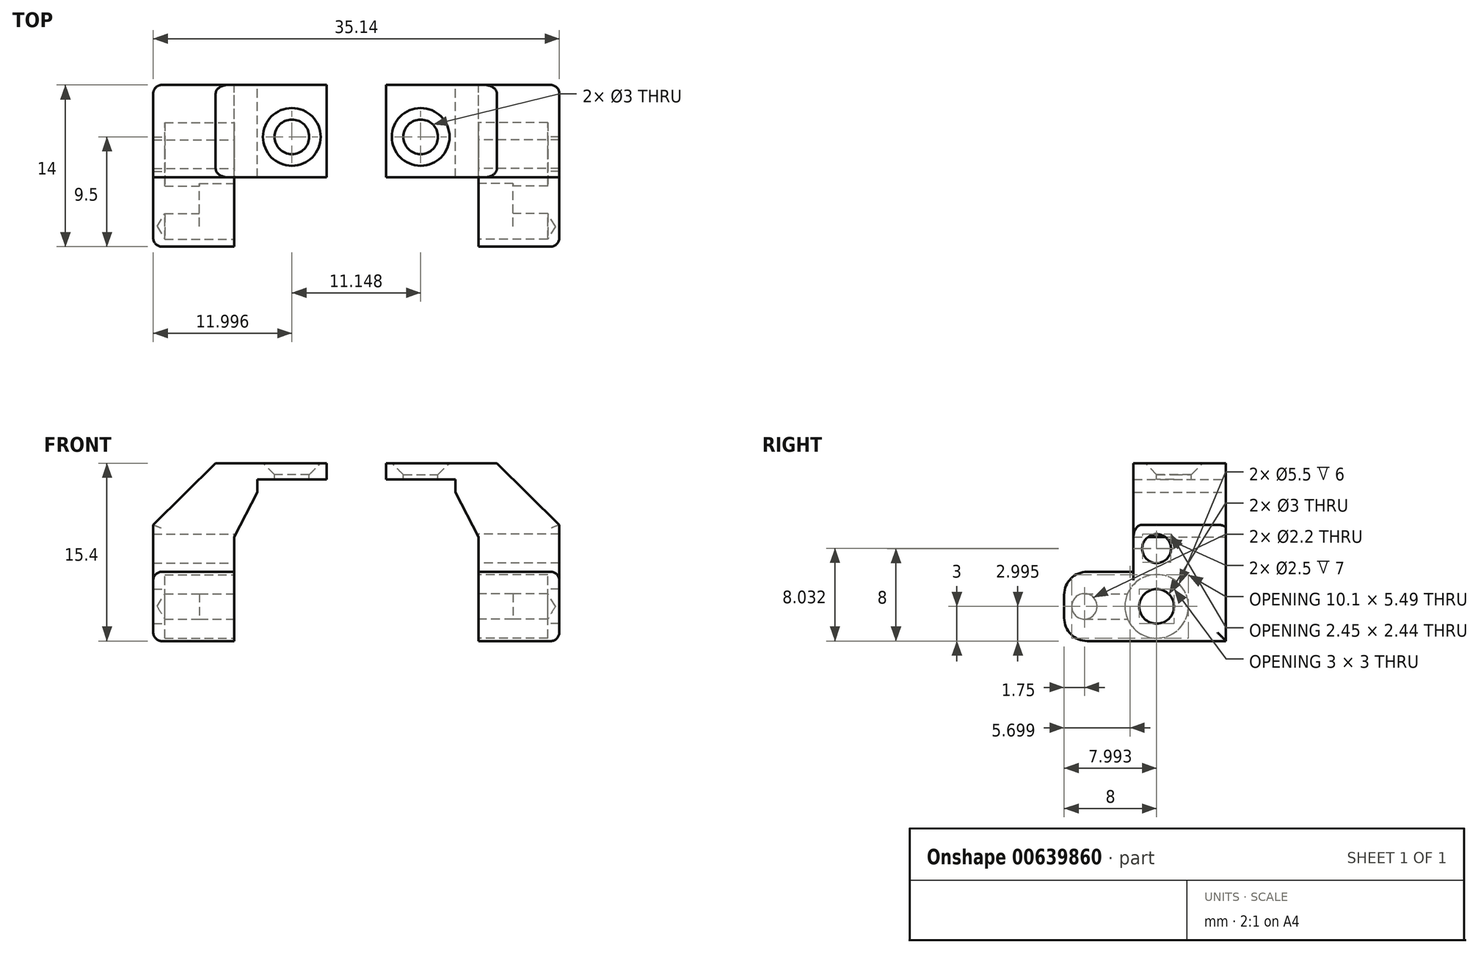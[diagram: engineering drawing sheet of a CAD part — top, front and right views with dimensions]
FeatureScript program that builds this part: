
annotation { "Feature Type Name" : "Feature", "Feature Type Description" : "" }
export const myFeature = defineFeature(function(context is Context, id is Id, definition is map)
    precondition{}
    {
        {
            var Q0;
            Q0=qCreatedBy(makeId("Front.planeOp"),FACE);
            var sketch = newSketch(context, id + "F0", { "sketchPlane" : qUnion([Q0])});
            skLineSegment(sketch, "E0", {"start": v(-10.57, 0) * mm, "end": v(-17.57, 0) * mm});
            skLineSegment(sketch, "E1", {"start": v(-17.57, 0) * mm, "end": v(-17.57, 10.07) * mm});
            skLineSegment(sketch, "E2", {"start": v(-17.57, 10.07) * mm, "end": v(-12.17, 15.4) * mm});
            skLineSegment(sketch, "E3", {"start": v(-12.17, 15.4) * mm, "end": v(-2.57, 15.4) * mm});
            skLineSegment(sketch, "E4", {"start": v(-2.57, 15.4) * mm, "end": v(-2.57, 14) * mm});
            skLineSegment(sketch, "E5", {"start": v(-2.57, 14) * mm, "end": v(-8.57, 14) * mm});
            skLineSegment(sketch, "E6", {"start": v(-10.57, 9) * mm, "end": v(-10.57, 0) * mm});
            skLineSegment(sketch, "E7", {"start": v(-8.57, 14) * mm, "end": v(-8.57, 12.88) * mm});
            skLineSegment(sketch, "E8", {"start": v(-8.57, 12.88) * mm, "end": v(-10.57, 9) * mm});
            skSolve(sketch);
        }
        {
            var Q0;
            Q0 = qSketchRegion(id + "F0", true);
            extrude(context, id + "F1", {"entities" : qUnion([Q0]), "depth" : 8 * mm, "offsetDistance" : 25 * mm});
        }
        {
            var Q0;
            Q0=makeQuery(id+"F1.opExtrude","SWEPT_FACE",FACE,{"disambiguationData":[OSD([sQuery(id+"F0.wireOp",EDGE,"E3")])]});
            var sketch = newSketch(context, id + "F2", { "sketchPlane" : qUnion([Q0])});
            skPoint(sketch, "E9.endSnap0", {"position": v(-5.57, -8) * mm});
            skLineSegment(sketch, "E10", {"start": v(-5.57, -8) * mm, "end": v(-5.57, -4.5) * mm});
            skCircle(sketch, "E11", {"center": v(-5.57, -4.5) * mm, "radius": 1.5 * mm});
            skSolve(sketch);
        }
        {
            var Q0;
            Q0=sQuery(id+"F2.wireOp",VERTEX,"E10.end");
            var Q1;
            Q1=makeQuery(id+"F1.opExtrude","SWEPT_BODY",BODY,{"disambiguationData":[OSD([sQuery(id+"F0.wireOp",EDGE,"E0"),sQuery(id+"F0.wireOp",EDGE,"E1"),sQuery(id+"F0.wireOp",EDGE,"E2"),sQuery(id+"F0.wireOp",EDGE,"E3"),sQuery(id+"F0.wireOp",EDGE,"E4"),sQuery(id+"F0.wireOp",EDGE,"E5"),sQuery(id+"F0.wireOp",EDGE,"E6"),sQuery(id+"F0.wireOp",EDGE,"E7"),sQuery(id+"F0.wireOp",EDGE,"E8")])]});
            hole(context, id + "F3", {"style" : HoleStyle.C_SINK, "endStyle" : HoleEndStyle.THROUGH, "holeDiameter" : 3 * mm, "cSinkDiameter" : 5 * mm, "cSinkAngle" : 90 * degree, "majorDiameter" : 5 * mm, "isTappedThrough" : true, "tappedDepth" : 12 * mm, "tapClearance" : 3, "locations" : qUnion([Q0]), "scope" : qUnion([Q1])});
        }
        {
            var Q0;
            Q0=makeQuery(id+"F1.opExtrude","SWEPT_FACE",FACE,{"disambiguationData":[OSD([sQuery(id+"F0.wireOp",EDGE,"E6")])]});
            var sketch = newSketch(context, id + "F4", { "sketchPlane" : qUnion([Q0])});
            skLineSegment(sketch, "E12", {"start": v(-8, 3) * mm, "end": v(-6, 3) * mm});
            skLineSegment(sketch, "E13", {"start": v(-6, 3) * mm, "end": v(-12.25, 3) * mm});
            skPoint(sketch, "E14", {"position": v(-12.25, 3) * mm});
            skCircle(sketch, "E15", {"center": v(-12.25, 3) * mm, "radius": 1.1 * mm});
            skLineSegment(sketch, "E16", {"start": v(-12.25, 4.1) * mm, "end": v(-6, 4.1) * mm});
            skLineSegment(sketch, "E17", {"start": v(-12.25, 1.9) * mm, "end": v(-6, 1.9) * mm});
            skLineSegment(sketch, "E18", {"start": v(-6, 1.9) * mm, "end": v(-6, 4.1) * mm});
            skLineSegment(sketch, "E19", {"start": v(-6, 3) * mm, "end": v(-6, 8) * mm});
            skSolve(sketch);
        }
        {
            var Q0;
            Q0=makeQuery(id+"F1.opExtrude","CAP_FACE",FACE,{"disambiguationData":[OSD([sQuery(id+"F0.wireOp",EDGE,"E0"),sQuery(id+"F0.wireOp",EDGE,"E1"),sQuery(id+"F0.wireOp",EDGE,"E2"),sQuery(id+"F0.wireOp",EDGE,"E3"),sQuery(id+"F0.wireOp",EDGE,"E4"),sQuery(id+"F0.wireOp",EDGE,"E5"),sQuery(id+"F0.wireOp",EDGE,"E6"),sQuery(id+"F0.wireOp",EDGE,"E7"),sQuery(id+"F0.wireOp",EDGE,"E8")])],"isStart":false});
            var sketch = newSketch(context, id + "F5", { "sketchPlane" : qUnion([Q0])});
            skLineSegment(sketch, "E20", {"start": v(-10.57, 6) * mm, "end": v(-17.57, 6) * mm});
            skSolve(sketch);
        }
        {
            var Q0;
            {var subQ0=sQuery(id+"F5.wireOp",EDGE,"E20");Q0=makeQuery(id+"F5.imprint","IMPRINT",FACE,{"disambiguationData":[TD([[makeQuery(id+"F5.imprint","IMPRINT",EDGE,{"derivedFrom":subQ0}),1.0]])]});}
            extrude(context, id + "F6", {"entities" : qUnion([Q0]), "operationType" : NewBodyOperationType.ADD, "depth" : 6 * mm, "offsetDistance" : 25 * mm});
        }
        {
            var Q0;
            Q0=sQuery(id+"F4.wireOp",VERTEX,"E12.end");
            var Q1;
            Q1=makeQuery(id+"F1.opExtrude","SWEPT_BODY",BODY,{"disambiguationData":[OSD([sQuery(id+"F0.wireOp",EDGE,"E0"),sQuery(id+"F0.wireOp",EDGE,"E1"),sQuery(id+"F0.wireOp",EDGE,"E2"),sQuery(id+"F0.wireOp",EDGE,"E3"),sQuery(id+"F0.wireOp",EDGE,"E4"),sQuery(id+"F0.wireOp",EDGE,"E5"),sQuery(id+"F0.wireOp",EDGE,"E6"),sQuery(id+"F0.wireOp",EDGE,"E7"),sQuery(id+"F0.wireOp",EDGE,"E8")])]});
            hole(context, id + "F7", {"style" : HoleStyle.C_BORE, "endStyle" : HoleEndStyle.THROUGH, "holeDiameter" : 3 * mm, "cBoreDiameter" : 5.5 * mm, "cBoreDepth" : 6 * mm, "majorDiameter" : 5 * mm, "isTappedThrough" : true, "tappedDepth" : 12 * mm, "tapClearance" : 3, "locations" : qUnion([Q0]), "scope" : qUnion([Q1])});
        }
        {
            var Q0;
            {var subQ0=sQuery(id+"F4.wireOp",EDGE,"E13");var subQ1=makeQuery(id+"F1.opExtrude","CAP_EDGE",EDGE,{"disambiguationData":[OSD([sQuery(id+"F0.wireOp",EDGE,"E6")])],"isStart":false});var subQ2=makeQuery(id+"F4.imprint","INTERSECT",VERTEX,{"derivedFrom":[subQ1,subQ0]});Q0=makeQuery(id+"F4.imprint","IMPRINT",FACE,{"disambiguationData":[TD([[makeQuery(id+"F4.imprint","IMPRINT",EDGE,{"disambiguationData":[TD([[subQ2,-1.0]])],"derivedFrom":subQ0}),-1.0]])]});}
            var Q1;
            {var subQ0=sQuery(id+"F4.wireOp",EDGE,"E13");var subQ1=makeQuery(id+"F1.opExtrude","CAP_EDGE",EDGE,{"disambiguationData":[OSD([sQuery(id+"F0.wireOp",EDGE,"E6")])],"isStart":false});var subQ2=makeQuery(id+"F4.imprint","INTERSECT",VERTEX,{"derivedFrom":[subQ1,subQ0]});Q1=makeQuery(id+"F4.imprint","IMPRINT",FACE,{"disambiguationData":[TD([[makeQuery(id+"F4.imprint","IMPRINT",EDGE,{"disambiguationData":[TD([[subQ2,-1.0]])],"derivedFrom":subQ0}),1.0]])]});}
            extrude(context, id + "F8", {"entities" : qUnion([Q0, Q1]), "operationType" : NewBodyOperationType.REMOVE, "oppositeDirection" : true, "depth" : 3 * mm, "offsetDistance" : 25 * mm});
        }
        {
            var Q0;
            Q0=sQuery(id+"F4.wireOp",VERTEX,"E14");
            var Q1;
            Q1=makeQuery(id+"F1.opExtrude","SWEPT_BODY",BODY,{"disambiguationData":[OSD([sQuery(id+"F0.wireOp",EDGE,"E0"),sQuery(id+"F0.wireOp",EDGE,"E1"),sQuery(id+"F0.wireOp",EDGE,"E2"),sQuery(id+"F0.wireOp",EDGE,"E3"),sQuery(id+"F0.wireOp",EDGE,"E4"),sQuery(id+"F0.wireOp",EDGE,"E5"),sQuery(id+"F0.wireOp",EDGE,"E6"),sQuery(id+"F0.wireOp",EDGE,"E7"),sQuery(id+"F0.wireOp",EDGE,"E8")])]});
            hole(context, id + "F9", {"style" : HoleStyle.SIMPLE, "endStyle" : HoleEndStyle.BLIND, "holeDiameter" : 2.2 * mm, "majorDiameter" : 5 * mm, "holeDepth" : 6 * mm, "isTappedThrough" : true, "tappedDepth" : 12 * mm, "tapClearance" : 3, "locations" : qUnion([Q0]), "scope" : qUnion([Q1])});
        }
        {
            var Q0;
            Q0=makeQuery(id+"F6.opExtrude","CAP_EDGE",EDGE,{"disambiguationData":[OSD([sQuery(id+"F5.wireOp",EDGE,"E20")])],"isStart":false});
            var Q1;
            Q1=makeQuery(id+"F6.opExtrude","CAP_EDGE",EDGE,{"disambiguationData":[OSD([sQuery(id+"F0.wireOp",EDGE,"E0")])],"isStart":false});
            fillet(context, id + "F10", {"entities" : qUnion([Q0, Q1]), "radius" : 2 * mm, "tangentPropagation" : true, "allowEdgeOverflow" : false});
        }
        {
            var Q0;
            Q0=makeQuery(id+"F1.opExtrude","CAP_EDGE",EDGE,{"disambiguationData":[OSD([sQuery(id+"F0.wireOp",EDGE,"E2")])],"isStart":true});
            var Q1;
            Q1=makeQuery(id+"F1.opExtrude","CAP_EDGE",EDGE,{"disambiguationData":[OSD([sQuery(id+"F0.wireOp",EDGE,"E2")])],"isStart":false});
            var Q2;
            Q2=makeQuery(id+"F1.opExtrude","CAP_EDGE",EDGE,{"disambiguationData":[OSD([sQuery(id+"F0.wireOp",EDGE,"E1")])],"isStart":true});
            var Q3;
            {var subQ0=sQuery(id+"F0.wireOp",EDGE,"E1");var subQ1=sQuery(id+"F0.wireOp",EDGE,"E0");Q3=makeQuery(id+"F6.boolean.opBoolean","MERGE",EDGE,{"derivedFrom":[makeQuery(id+"F1.opExtrude","SWEPT_EDGE",EDGE,{"disambiguationData":[OSD([subQ1,subQ0])]}),makeQuery(id+"F6.opExtrude","SWEPT_EDGE",EDGE,{"disambiguationData":[OSD([subQ1,subQ0])]})]});}
            fillet(context, id + "F11", {"entities" : qUnion([Q0, Q1, Q2, Q3]), "radius" : 0.75 * mm, "tangentPropagation" : true, "allowEdgeOverflow" : false});
        }
        {
            var Q0;
            Q0=sQuery(id+"F4.wireOp",VERTEX,"E19.end");
            var Q1;
            Q1=makeQuery(id+"F1.opExtrude","SWEPT_BODY",BODY,{"disambiguationData":[OSD([sQuery(id+"F0.wireOp",EDGE,"E0"),sQuery(id+"F0.wireOp",EDGE,"E1"),sQuery(id+"F0.wireOp",EDGE,"E2"),sQuery(id+"F0.wireOp",EDGE,"E3"),sQuery(id+"F0.wireOp",EDGE,"E4"),sQuery(id+"F0.wireOp",EDGE,"E5"),sQuery(id+"F0.wireOp",EDGE,"E6"),sQuery(id+"F0.wireOp",EDGE,"E7"),sQuery(id+"F0.wireOp",EDGE,"E8")])]});
            hole(context, id + "F12", {"style" : HoleStyle.SIMPLE, "endStyle" : HoleEndStyle.THROUGH, "holeDiameter" : 2.5 * mm, "majorDiameter" : 5 * mm, "isTappedThrough" : true, "tappedDepth" : 12 * mm, "tapClearance" : 3, "locations" : qUnion([Q0]), "scope" : qUnion([Q1])});
        }
        {
            var Q0;
            Q0=makeQuery(id+"F1.opExtrude","SWEPT_BODY",BODY,{"disambiguationData":[OSD([sQuery(id+"F0.wireOp",EDGE,"E0"),sQuery(id+"F0.wireOp",EDGE,"E1"),sQuery(id+"F0.wireOp",EDGE,"E2"),sQuery(id+"F0.wireOp",EDGE,"E3"),sQuery(id+"F0.wireOp",EDGE,"E4"),sQuery(id+"F0.wireOp",EDGE,"E5"),sQuery(id+"F0.wireOp",EDGE,"E6"),sQuery(id+"F0.wireOp",EDGE,"E7"),sQuery(id+"F0.wireOp",EDGE,"E8")])]});
            var Q1;
            Q1=qCreatedBy(makeId("Right.planeOp"),FACE);
            mirror(context, id + "F13", {"entities" : qUnion([Q0]), "mirrorPlane" : qUnion([Q1])});
        }
    });
